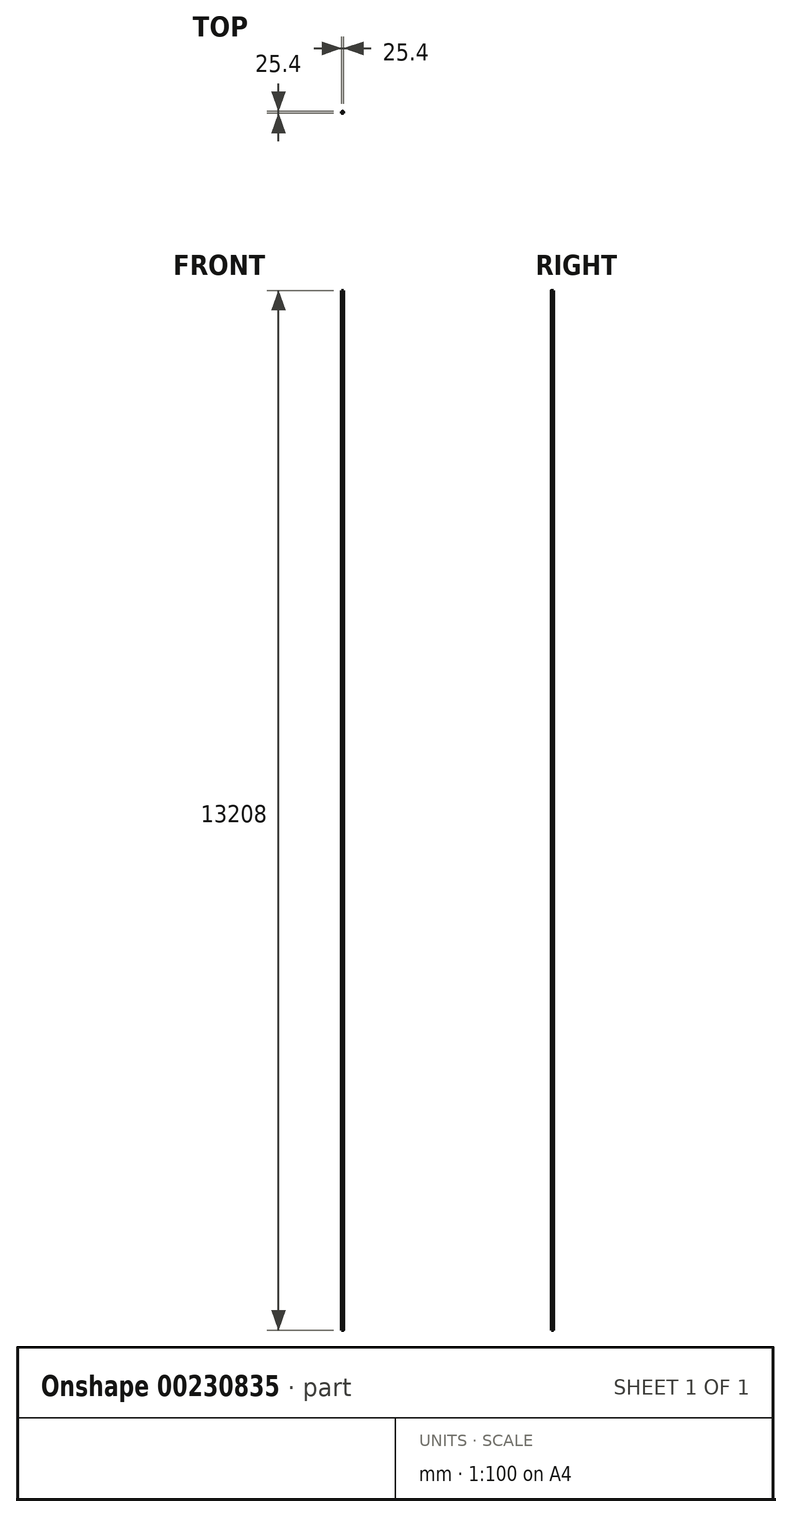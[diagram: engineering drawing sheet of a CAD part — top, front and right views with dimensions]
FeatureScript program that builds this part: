
annotation { "Feature Type Name" : "Feature", "Feature Type Description" : "" }
export const myFeature = defineFeature(function(context is Context, id is Id, definition is map)
    precondition{}
    {
        {
            var Q0;
            Q0=qCreatedBy(makeId("Top.planeOp"),FACE);
            var sketch = newSketch(context, id + "F0", { "sketchPlane" : qUnion([Q0])});
            skCircle(sketch, "E0", {"center": v(-40.13, 37.05) * mm, "radius": 12.7 * mm});
            skCircle(sketch, "E1", {"center": v(-40.13, 37.05) * mm, "radius": 9.32 * mm});
            skSolve(sketch);
        }
        {
            var Q0;
            Q0 = qSketchRegion(id + "F0", true);
            extrude(context, id + "F1", {"entities" : qUnion([Q0]), "depth" : 13208 * mm});
        }
    });
